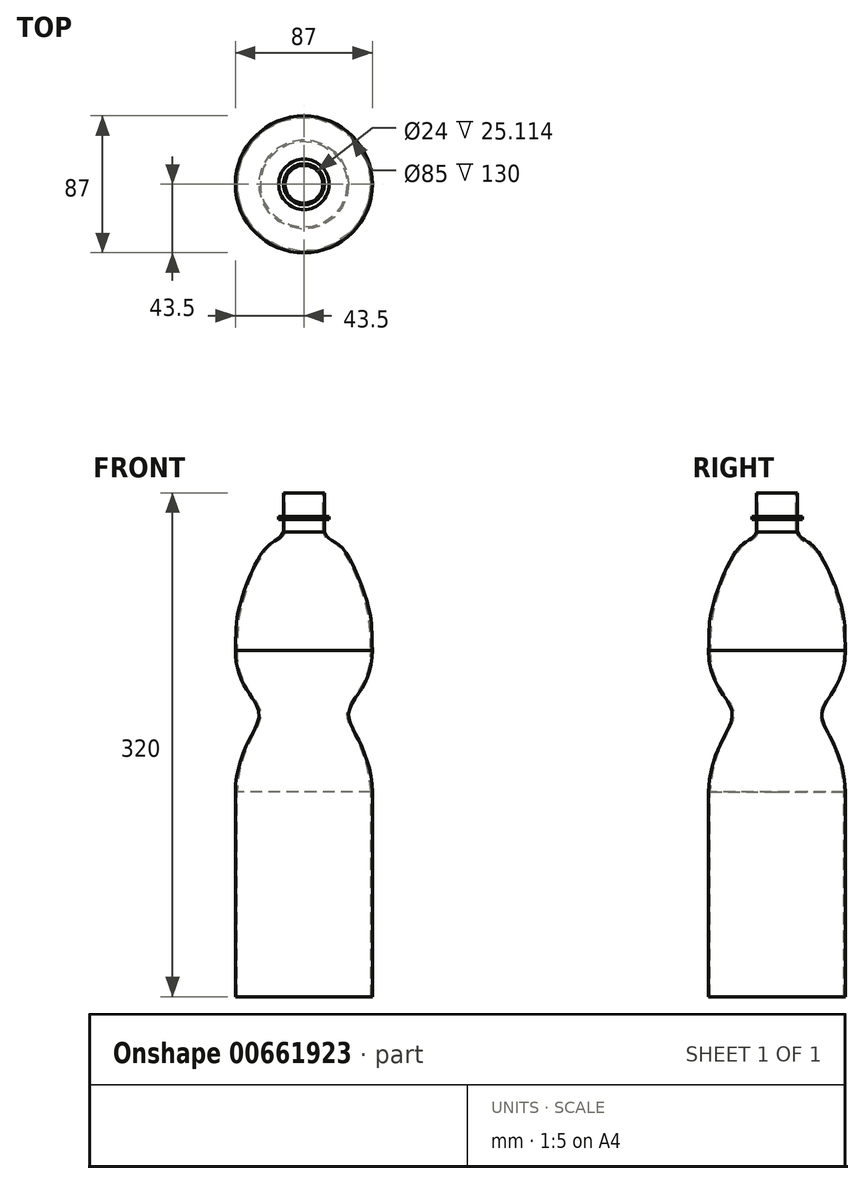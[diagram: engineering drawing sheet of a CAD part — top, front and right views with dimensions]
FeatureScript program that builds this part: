
annotation { "Feature Type Name" : "Feature", "Feature Type Description" : "" }
export const myFeature = defineFeature(function(context is Context, id is Id, definition is map)
    precondition{}
    {
        {
            var Q0;
            Q0=qCreatedBy(makeId("Front.planeOp"),FACE);
            var sketch = newSketch(context, id + "F0", { "sketchPlane" : qUnion([Q0])});
            skLineSegment(sketch, "E0", {"start": v(0, 0) * mm, "end": v(0, -350) * mm, "construction": true});
            skLineSegment(sketch, "E1", {"start": v(0, -350) * mm, "end": v(23.5, -350) * mm});
            skLineSegment(sketch, "E2", {"start": v(13, 0) * mm, "end": v(13, -15) * mm});
            skLineSegment(sketch, "E3", {"start": v(13, -15) * mm, "end": v(16, -15) * mm});
            skLineSegment(sketch, "E4", {"start": v(16, -15) * mm, "end": v(16, -17) * mm});
            skLineSegment(sketch, "E5", {"start": v(16, -17) * mm, "end": v(13, -17) * mm});
            skLineSegment(sketch, "E6", {"start": v(13, -17) * mm, "end": v(13, -25) * mm});
            skLineSegment(sketch, "E7", {"start": v(43.5, -330) * mm, "end": v(43.5, -190) * mm});
            skFitSpline(sketch, "E8", {"points": [v(13, -25) * mm, v(23.3, -33.97) * mm, v(41.61, -75.05) * mm, v(43.5, -100) * mm], "startDerivative": vector(26.94, -62.58) * mm, "endDerivative": vector(5.84, -102.9) * mm});
            skPoint(sketch, "E9.visualSharp", {"position": v(43.5, -350) * mm});
            skArc(sketch, "E9.filletArc", {"start": v(23.5, -350) * mm, "mid": v(37.64, -344.14) * mm, "end": v(43.5, -330) * mm});
            skPoint(sketch, "E10", {"position": v(43.5, -190) * mm});
            skPoint(sketch, "E11", {"position": v(28.5, -140) * mm});
            skFitSpline(sketch, "E12", {"points": [v(43.5, -100) * mm, v(37.2, -123.66) * mm, v(28.5, -140) * mm, v(35.25, -157.94) * mm, v(43.5, -190) * mm], "startDerivative": vector(0.16, -108.9) * mm, "endDerivative": vector(-0.14, -116.28) * mm});
            skLineSegment(sketch, "E13", {"start": v(0, -350) * mm, "end": v(0, -349) * mm});
            skLineSegment(sketch, "E14", {"start": v(0, -349) * mm, "end": v(23.5, -349) * mm});
            skLineSegment(sketch, "E15", {"start": v(42.5, -330) * mm, "end": v(42.5, -190) * mm});
            skLineSegment(sketch, "E16", {"start": v(0, 0) * mm, "end": v(0, -1) * mm});
            skLineSegment(sketch, "E17", {"start": v(12, -1) * mm, "end": v(12, -25.11) * mm});
            skPoint(sketch, "E18.visualSharp", {"position": v(42.5, -349) * mm});
            skArc(sketch, "E18.filletArc", {"start": v(23.5, -349) * mm, "mid": v(36.94, -343.44) * mm, "end": v(42.5, -330) * mm});
            skPoint(sketch, "E19", {"position": v(27.5, -140) * mm});
            skPoint(sketch, "E20", {"position": v(42.5, -100) * mm});
            skFitSpline(sketch, "E21", {"points": [v(42.5, -190) * mm, v(34.43, -157.94) * mm, v(27.5, -140) * mm, v(36.38, -123.66) * mm, v(42.5, -100) * mm], "startDerivative": vector(-4.2, 116.62) * mm, "endDerivative": vector(-2.78, 97.68) * mm});
            skFitSpline(sketch, "E22", {"points": [v(42.5, -100) * mm, v(40.35, -75.05) * mm, v(22.14, -33.97) * mm, v(12, -25.11) * mm], "startDerivative": vector(-3.15, 69.37) * mm, "endDerivative": vector(-24.82, 65.51) * mm});
            skLineSegment(sketch, "E23", {"start": v(12, -1) * mm, "end": v(12, 0) * mm});
            skLineSegment(sketch, "E24", {"start": v(12, 0) * mm, "end": v(13, 0) * mm});
            skSolve(sketch);
        }
        {
            var Q0;
            Q0 = qSketchRegion(id + "F0", true);
            var Q1;
            Q1=sQuery(id+"F0.wireOp",EDGE,"E0");
            revolve(context, id + "F1", {"entities" : qUnion([Q0]), "axis" : qUnion([Q1]), "revolveType" : RevolveType.FULL});
        }
        {
            var Q0;
            Q0=qCreatedBy(makeId("Front.planeOp"),FACE);
            var sketch = newSketch(context, id + "F2", { "sketchPlane" : qUnion([Q0])});
            skLineSegment(sketch, "E25.bottom", {"start": v(-45.01, -320) * mm, "end": v(45.75, -320) * mm});
            skLineSegment(sketch, "E25.top", {"start": v(-45.01, -350) * mm, "end": v(45.75, -350) * mm});
            skLineSegment(sketch, "E25.left", {"start": v(-45.01, -320) * mm, "end": v(-45.01, -350) * mm});
            skLineSegment(sketch, "E25.right", {"start": v(45.75, -320) * mm, "end": v(45.75, -350) * mm});
            skSolve(sketch);
        }
        {
            var Q0;
            Q0 = qSketchRegion(id + "F2", true);
            extrude(context, id + "F3", {"entities" : qUnion([Q0]), "operationType" : NewBodyOperationType.REMOVE, "depth" : 100 * mm, "offsetDistance" : 25 * mm, "symmetric" : true});
        }
    });
